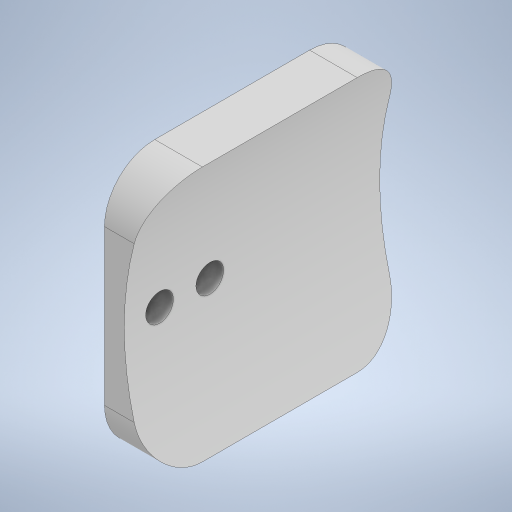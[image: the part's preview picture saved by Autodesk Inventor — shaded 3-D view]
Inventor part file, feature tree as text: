
AUTODESK INVENTOR PART (.ipt)
format: ipt  version: 2023 (Build 270158030, 158C)  size: 241,664 bytes
history: native  units: in
note: dims shown in document units (in); Inventor stores cm internally (conversion verified against a paired STEP export)
features: extrude x2, sketch x2, fillet x1
ambient origin geometry x8: Origin, YZ Plane, XZ Plane, XY Plane, X Axis, Y Axis, Z Axis, Center Point
bodies: Solid1 (feature_tree)
feature tree (5):
  extrude  "Extrusion1"  Depth=2.5591in
  extrude  "Extrusion2"  Depth=0.3937in TaperAngle=0.0deg
  fillet  "Fillet1"  [1 undecoded]
  sketch  "Sketch1"  dims[d0=4.808in d1=2.5591in]
  sketch  "Sketch2"  dims[d2=2.0in d3=2.0in d4=0.0in d6=0.0in d7=0.0in d8=0.2165in d9=0.2756in d10=0.3937in d11=0.3937in]
note: 1 required parameter value undecoded (feature->parameter linkage not recoverable at this tier; creation-order binding heuristic only, values carry confidence <= 0.55)
